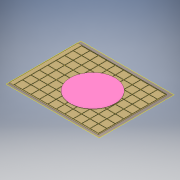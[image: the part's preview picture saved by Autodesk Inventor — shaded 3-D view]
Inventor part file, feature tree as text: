
AUTODESK INVENTOR PART (.ipt)
format: ipt  version: 2019 (Build 230136000, 136)  size: 418,816 bytes
history: native  units: mm
features: extrude x3, sketch x3, pattern_linear x1, plane x1
ambient origin geometry x8: Origin, YZ Plane, XZ Plane, XY Plane, X Axis, Y Axis, Z Axis, Center Point
bodies: Solid1 (feature_tree)
feature tree (8):
  extrude  "Extrusion1"  Depth=77.0mm
  extrude  "Extrusion2"  Depth=10.0mm
  pattern_linear  "Rectangular Pattern1"  Spacing1=0.5mm  [1 undecoded]
  plane  "Work Plane1"
  extrude  "Extrusion4"  Depth=0.15mm TaperAngle=0.0deg
  sketch  "Sketch1"  dims[d0=100.0mm d1=77.0mm]
  sketch  "Sketch2"  dims[d2=1.0mm d3=0.0mm d4=10.0mm]
  sketch  "Sketch4"  dims[d5=10.0mm d6=0.5mm d7=0.15mm d8=0.0mm d9=100.0mm d11=9.5mm d12=80.0mm d14=9.5mm d20=0.0mm d21=50.4mm d22=45.0mm d23=38.5mm d24=0.3mm d25=0.0mm]
note: 1 required parameter value undecoded (feature->parameter linkage not recoverable at this tier; creation-order binding heuristic only, values carry confidence <= 0.55)
